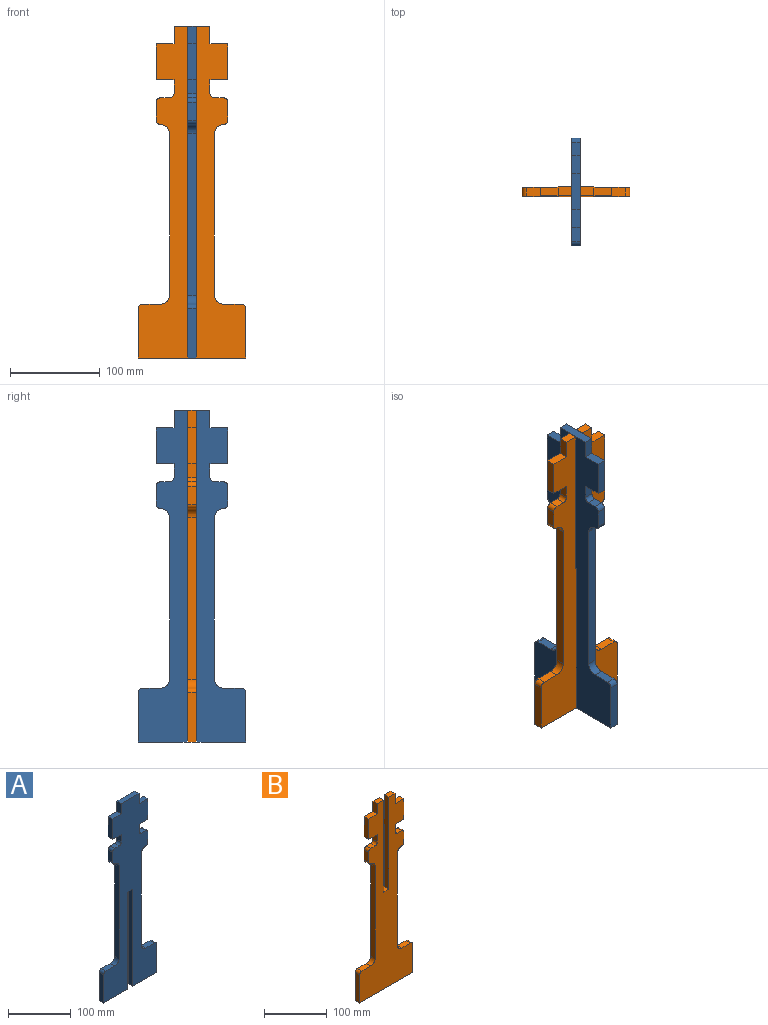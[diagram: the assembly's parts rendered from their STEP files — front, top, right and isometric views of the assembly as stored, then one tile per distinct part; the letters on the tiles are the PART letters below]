
ASSEMBLY  parts=2 mates=1
PART A: 40 faces, bbox 120x10x370 mm
  f0: plane 20x10mm, normal (-1,0,0), area 200mm2, adj f1,f37,f38,f39
  f1: plane 20x10mm, normal (0,0,1), area 200mm2, adj f0,f2,f38,f39
  f2: plane 40x10mm, normal (-1,0,0), area 400mm2, adj f1,f3,f38,f39
  f3: plane 20x10mm, normal (0,0,-1), area 200mm2, adj f2,f4,f38,f39
  f4: plane 15x10mm, normal (-1,0,0), area 150mm2, adj f3,f5,f38,f39
  f5: cylinder r=5mm len=10mm, axis (0,-1,0), area 78.5mm2, adj f4,f6,f38,f39
  f6: plane 10x10mm, normal (0,0,1), area 100mm2, adj f5,f7,f38,f39
  f7: cylinder r=5mm len=10mm, axis (0,-1,0), area 78.5mm2, adj f6,f8,f38,f39
  f8: plane 20x10mm, normal (-1,0,0), area 200mm2, adj f7,f9,f38,f39
  f9: cylinder r=5mm len=10mm, axis (0,-1,0), area 78.5mm2, adj f8,f10,f38,f39
  f10: cylinder r=10mm len=10mm, axis (0,-1,0), area 157.1mm2, adj f9,f11,f38,f39
  f11: plane 180x10mm, normal (-1,0,0), area 1800mm2, adj f10,f12,f38,f39
  f12: cylinder r=10mm len=10mm, axis (0,-1,0), area 157.1mm2, adj f11,f13,f38,f39
  f13: plane 20x10mm, normal (0,0,1), area 200mm2, adj f12,f14,f38,f39
  f14: cylinder r=5mm len=10mm, axis (0,-1,0), area 78.5mm2, adj f13,f15,f38,f39
  f15: plane 55x10mm, normal (-1,0,0), area 550mm2, adj f14,f16,f38,f39
  f16: plane 54.5x10mm, normal (0,0,-1), area 545mm2, adj f15,f17,f38,f39
  f17: plane 190x10mm, normal (1,0,0), area 1900mm2, adj f16,f18,f38,f39
  f18: plane 11x10mm, normal (0,0,-1), area 110mm2, adj f17,f19,f38,f39
  f19: plane 190x10mm, normal (-1,0,0), area 1900mm2, adj f18,f20,f38,f39
  f20: plane 54.5x10mm, normal (0,0,-1), area 545mm2, adj f19,f21,f38,f39
  f21: plane 55x10mm, normal (1,0,0), area 550mm2, adj f20,f22,f38,f39
  f22: cylinder r=5mm len=10mm, axis (0,-1,0), area 78.5mm2, adj f21,f23,f38,f39
  f23: plane 20x10mm, normal (0,0,1), area 200mm2, adj f22,f24,f38,f39
  f24: cylinder r=10mm len=10mm, axis (0,-1,0), area 157.1mm2, adj f23,f25,f38,f39
  f25: plane 180x10mm, normal (1,0,0), area 1800mm2, adj f24,f26,f38,f39
  f26: cylinder r=10mm len=10mm, axis (0,-1,0), area 157.1mm2, adj f25,f27,f38,f39
  f27: cylinder r=5mm len=10mm, axis (0,-1,0), area 78.5mm2, adj f26,f28,f38,f39
  f28: plane 20x10mm, normal (1,0,0), area 200mm2, adj f27,f29,f38,f39
  f29: cylinder r=5mm len=10mm, axis (0,-1,0), area 78.5mm2, adj f28,f30,f38,f39
  f30: plane 10x10mm, normal (0,0,1), area 100mm2, adj f29,f31,f38,f39
  f31: cylinder r=5mm len=10mm, axis (0,-1,0), area 78.5mm2, adj f30,f32,f38,f39
  f32: plane 15x10mm, normal (1,0,0), area 150mm2, adj f31,f33,f38,f39
  f33: plane 20x10mm, normal (0,0,-1), area 200mm2, adj f32,f34,f38,f39
  f34: plane 40x10mm, normal (1,0,0), area 400mm2, adj f33,f35,f38,f39
  f35: plane 20x10mm, normal (0,0,1), area 200mm2, adj f34,f36,f38,f39
  f36: plane 20x10mm, normal (1,0,0), area 200mm2, adj f35,f37,f38,f39
  f37: plane 40x10mm, normal (0,0,1), area 400mm2, adj f0,f36,f38,f39
  f38: plane 370x120mm, normal (0,1,0), area 22374.4mm2, adj f0,f1,f2,f3,f4,f5,f6,f7
  f39: plane 370x120mm, normal (0,-1,0), area 22374.4mm2, adj f0,f1,f2,f3,f4,f5,f6,f7
PART B: 40 faces, bbox 120x10x370 mm
  f0: plane 20x10mm, normal (-1,0,0), area 200mm2, adj f1,f37,f38,f39
  f1: plane 20x10mm, normal (0,0,1), area 200mm2, adj f0,f2,f38,f39
  f2: plane 40x10mm, normal (-1,0,0), area 400mm2, adj f1,f3,f38,f39
  f3: plane 20x10mm, normal (0,0,-1), area 200mm2, adj f2,f4,f38,f39
  f4: plane 15x10mm, normal (-1,0,0), area 150mm2, adj f3,f5,f38,f39
  f5: cylinder r=5mm len=10mm, axis (0,1,0), area 78.5mm2, adj f4,f6,f38,f39
  f6: plane 10x10mm, normal (0,0,1), area 100mm2, adj f5,f7,f38,f39
  f7: cylinder r=5mm len=10mm, axis (0,1,0), area 78.5mm2, adj f6,f8,f38,f39
  f8: plane 20x10mm, normal (-1,0,0), area 200mm2, adj f7,f9,f38,f39
  f9: cylinder r=5mm len=10mm, axis (0,1,0), area 78.5mm2, adj f8,f10,f38,f39
  f10: cylinder r=10mm len=10mm, axis (0,1,0), area 157.1mm2, adj f9,f11,f38,f39
  f11: plane 180x10mm, normal (-1,0,0), area 1800mm2, adj f10,f12,f38,f39
  f12: cylinder r=10mm len=10mm, axis (0,1,0), area 157.1mm2, adj f11,f13,f38,f39
  f13: plane 20x10mm, normal (0,0,1), area 200mm2, adj f12,f14,f38,f39
  f14: cylinder r=5mm len=10mm, axis (0,1,0), area 78.5mm2, adj f13,f15,f38,f39
  f15: plane 55x10mm, normal (-1,0,0), area 550mm2, adj f14,f16,f38,f39
  f16: plane 120x10mm, normal (0,0,-1), area 1200mm2, adj f15,f17,f38,f39
  f17: plane 55x10mm, normal (1,0,0), area 550mm2, adj f16,f18,f38,f39
  f18: cylinder r=5mm len=10mm, axis (0,1,0), area 78.5mm2, adj f17,f19,f38,f39
  f19: plane 20x10mm, normal (0,0,1), area 200mm2, adj f18,f20,f38,f39
  f20: cylinder r=10mm len=10mm, axis (0,1,0), area 157.1mm2, adj f19,f21,f38,f39
  f21: plane 180x10mm, normal (1,0,0), area 1800mm2, adj f20,f22,f38,f39
  f22: cylinder r=10mm len=10mm, axis (0,1,0), area 157.1mm2, adj f21,f23,f38,f39
  f23: cylinder r=5mm len=10mm, axis (0,1,0), area 78.5mm2, adj f22,f24,f38,f39
  f24: plane 20x10mm, normal (1,0,0), area 200mm2, adj f23,f25,f38,f39
  f25: cylinder r=5mm len=10mm, axis (0,1,0), area 78.5mm2, adj f24,f26,f38,f39
  f26: plane 10x10mm, normal (0,0,1), area 100mm2, adj f25,f27,f38,f39
  f27: cylinder r=5mm len=10mm, axis (0,1,0), area 78.5mm2, adj f26,f28,f38,f39
  f28: plane 15x10mm, normal (1,0,0), area 150mm2, adj f27,f29,f38,f39
  f29: plane 20x10mm, normal (0,0,-1), area 200mm2, adj f28,f30,f38,f39
  f30: plane 40x10mm, normal (1,0,0), area 400mm2, adj f29,f31,f38,f39
  f31: plane 20x10mm, normal (0,0,1), area 200mm2, adj f30,f32,f38,f39
  f32: plane 20x10mm, normal (1,0,0), area 200mm2, adj f31,f33,f38,f39
  f33: plane 14.5x10mm, normal (0,0,1), area 145mm2, adj f32,f34,f38,f39
  f34: plane 180x10mm, normal (-1,0,0), area 1800mm2, adj f33,f35,f38,f39
  f35: plane 11x10mm, normal (0,0,1), area 110mm2, adj f34,f36,f38,f39
  f36: plane 180x10mm, normal (1,0,0), area 1800mm2, adj f35,f37,f38,f39
  f37: plane 14.5x10mm, normal (0,0,1), area 145mm2, adj f0,f36,f38,f39
  f38: plane 370x120mm, normal (0,-1,0), area 22484.4mm2, adj f0,f1,f2,f3,f4,f5,f6,f7
  f39: plane 370x120mm, normal (0,1,0), area 22484.4mm2, adj f0,f1,f2,f3,f4,f5,f6,f7
PLACE A rot(axis=(0,0,1),90deg) t=(-228.65,-49.7,-27.2)mm
PLACE B t=(-233.65,-44.7,-27.2)mm
MATE fastened A.f18 <-> B.f35  axis (0,0,-1) through (-233.65,-49.7,132.8)mm
